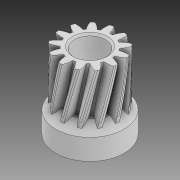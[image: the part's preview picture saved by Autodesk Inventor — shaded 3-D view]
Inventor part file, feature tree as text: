
AUTODESK INVENTOR PART (.ipt)
format: ipt  version: 2020 (Build 240168000, 168)  size: 612,352 bytes
history: native  units: mm
features: sketch x3, other x2, extrude x2, chamfer x2, revolve x1
ambient origin geometry x8: Origin, YZ Plane, XZ Plane, XY Plane, X Axis, Y Axis, Z Axis, Center Point
bodies: Solid1 (feature_tree)
feature tree (10):
  revolve  "Revolution1"  [1 undecoded]
  other  "Spur Gear Teeth1"
  extrude  "Extrusion1"  Depth=13.0mm
  extrude  "Extrusion2"  Depth=12.0mm
  chamfer  "Chamfer1"  Distance=3.55mm
  chamfer  "Chamfer2"  Distance=6.0mm
  sketch  "Sketch1"  dims[d0=4.1mm d2=8.0mm]
  other  "Spur Gear2"
  sketch  "Sketch2"  dims[d3=9.0mm d4=13.0mm]
  sketch  "Sketch3"  dims[d5=90.0deg d6=12.0mm d7=3.55mm d8=2.3mm d9=5.7mm d10=6.0mm d11=0.0mm d12=2.85mm d13=3.2mm d14=6.0mm d15=0.0mm d16=2.5mm d17=2.0mm d18=45.0deg d19=0.5mm d20=2.0mm d21=45.0deg]
note: 1 required parameter value undecoded (feature->parameter linkage not recoverable at this tier; creation-order binding heuristic only, values carry confidence <= 0.55)
